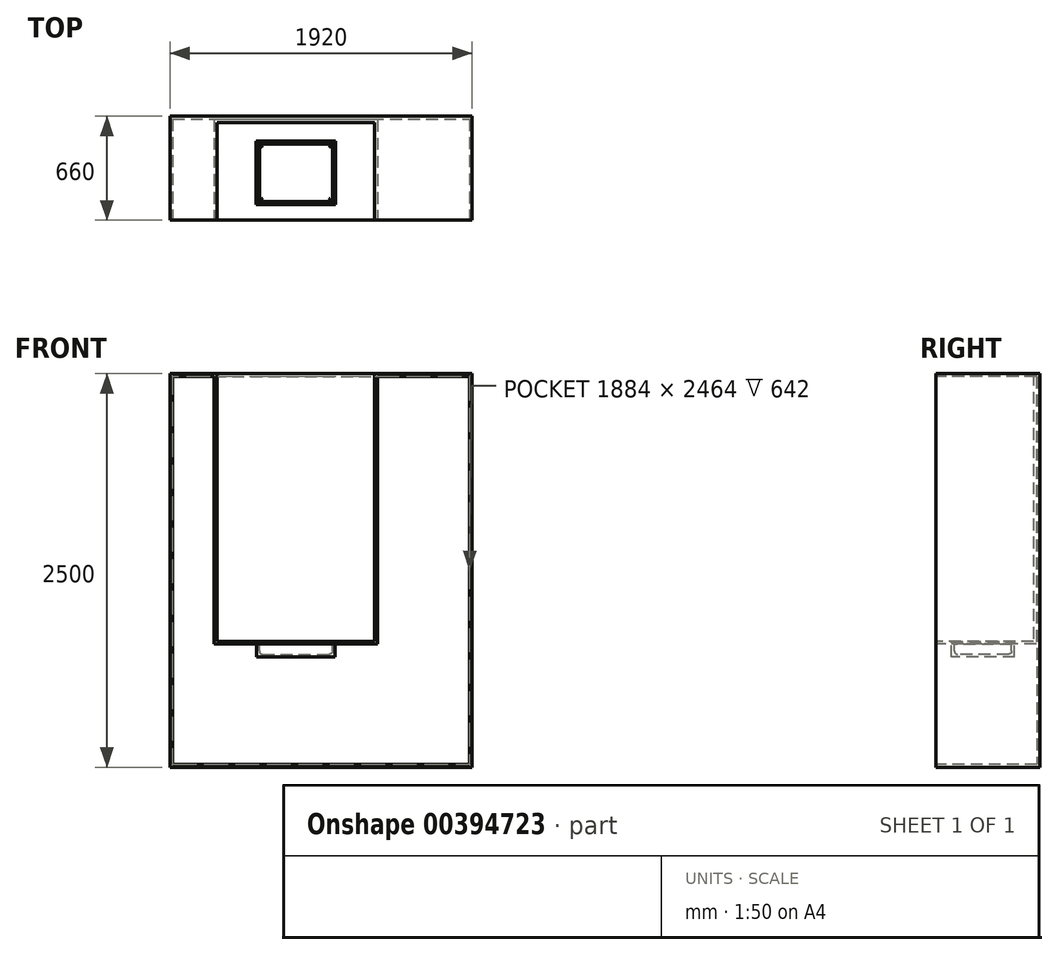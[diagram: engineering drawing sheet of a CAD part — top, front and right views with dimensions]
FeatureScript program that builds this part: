
annotation { "Feature Type Name" : "Feature", "Feature Type Description" : "" }
export const myFeature = defineFeature(function(context is Context, id is Id, definition is map)
    precondition{}
    {
        {
            var Q0;
            Q0=qCreatedBy(makeId("Top.planeOp"),FACE);
            var sketch = newSketch(context, id + "F0", { "sketchPlane" : qUnion([Q0])});
            skLineSegment(sketch, "E0.bottom", {"start": v(-310, 330) * mm, "end": v(310, 330) * mm});
            skLineSegment(sketch, "E0.top", {"start": v(-310, -330) * mm, "end": v(310, -330) * mm});
            skLineSegment(sketch, "E0.left", {"start": v(-310, 330) * mm, "end": v(-310, -330) * mm});
            skLineSegment(sketch, "E0.right", {"start": v(310, 330) * mm, "end": v(310, -330) * mm});
            skPoint(sketch, "E0.middle", {"position": v(0, 0) * mm});
            skLineSegment(sketch, "E1.bottom", {"start": v(-310, 330) * mm, "end": v(-1310, 330) * mm});
            skLineSegment(sketch, "E1.top", {"start": v(-310, -330) * mm, "end": v(-1310, -330) * mm});
            skLineSegment(sketch, "E1.right", {"start": v(-1310, 330) * mm, "end": v(-1310, -330) * mm});
            skLineSegment(sketch, "E2.bottom", {"start": v(-1310, 330) * mm, "end": v(-1610, 330) * mm});
            skLineSegment(sketch, "E2.top", {"start": v(-1310, -330) * mm, "end": v(-1610, -330) * mm});
            skLineSegment(sketch, "E2.right", {"start": v(-1610, 330) * mm, "end": v(-1610, -330) * mm});
            skSolve(sketch);
        }
        {
            var Q0;
            Q0=makeQuery(id+"F0.imprint","IMPRINT",FACE,{"disambiguationData":[TD([[makeQuery(id+"F0.imprint","IMPRINT",EDGE,{"derivedFrom":sQuery(id+"F0.wireOp",EDGE,"E0.bottom")}),-1.0]])]});
            extrude(context, id + "F1", {"entities" : qUnion([Q0]), "depth" : 2500 * mm});
        }
        {
            var Q0;
            Q0=makeQuery(id+"F0.imprint","IMPRINT",FACE,{"disambiguationData":[TD([[makeQuery(id+"F0.imprint","IMPRINT",EDGE,{"derivedFrom":sQuery(id+"F0.wireOp",EDGE,"E1.bottom")}),1.0]])]});
            extrude(context, id + "F2", {"entities" : qUnion([Q0]), "operationType" : NewBodyOperationType.ADD, "depth" : 800 * mm});
        }
        {
            var Q0;
            Q0=makeQuery(id+"F0.imprint","IMPRINT",FACE,{"disambiguationData":[TD([[makeQuery(id+"F0.imprint","IMPRINT",EDGE,{"derivedFrom":sQuery(id+"F0.wireOp",EDGE,"E2.bottom")}),1.0]])]});
            extrude(context, id + "F3", {"entities" : qUnion([Q0]), "operationType" : NewBodyOperationType.ADD, "depth" : 2500 * mm});
        }
        {
            var Q0;
            Q0=makeQuery(id+"F2.opExtrude","CAP_FACE",FACE,{"disambiguationData":[OSD([sQuery(id+"F0.wireOp",EDGE,"E1.bottom"),sQuery(id+"F0.wireOp",EDGE,"E1.top"),sQuery(id+"F0.wireOp",EDGE,"E0.left"),sQuery(id+"F0.wireOp",EDGE,"E1.right")])],"isStart":false});
            var sketch = newSketch(context, id + "F4", { "sketchPlane" : qUnion([Q0])});
            skLineSegment(sketch, "E3.bottom", {"start": v(-310, 330) * mm, "end": v(-1310, 330) * mm});
            skLineSegment(sketch, "E3.top", {"start": v(-310, 290) * mm, "end": v(-1310, 290) * mm});
            skLineSegment(sketch, "E3.left", {"start": v(-310, 330) * mm, "end": v(-310, 290) * mm});
            skLineSegment(sketch, "E3.right", {"start": v(-1310, 330) * mm, "end": v(-1310, 290) * mm});
            skSolve(sketch);
        }
        {
            var Q0;
            Q0=makeQuery(id+"F4.imprint","IMPRINT",FACE,{"disambiguationData":[TD([[makeQuery(id+"F4.imprint","IMPRINT",EDGE,{"derivedFrom":sQuery(id+"F4.wireOp",EDGE,"E3.bottom")}),1.0]])]});
            extrude(context, id + "F5", {"entities" : qUnion([Q0]), "operationType" : NewBodyOperationType.ADD, "depth" : 1700 * mm});
        }
        {
            var Q0;
            Q0=makeQuery(id+"F3.boolean.opBoolean","MERGE",FACE,{"derivedFrom":[makeQuery(id+"F2.boolean.opBoolean","MERGE",FACE,{"derivedFrom":[makeQuery(id+"F1.opExtrude","SWEPT_FACE",FACE,{"disambiguationData":[OSD([sQuery(id+"F0.wireOp",EDGE,"E0.top")])]}),makeQuery(id+"F2.opExtrude","SWEPT_FACE",FACE,{"disambiguationData":[OSD([sQuery(id+"F0.wireOp",EDGE,"E1.top")])]})]}),makeQuery(id+"F3.opExtrude","SWEPT_FACE",FACE,{"disambiguationData":[OSD([sQuery(id+"F0.wireOp",EDGE,"E2.top")])]})]});
            shell(context, id + "F6", {"entities" : qUnion([Q0]), "thickness" : 18 * mm});
        }
        {
            var Q0;
            Q0=makeQuery(id+"F2.opExtrude","CAP_FACE",FACE,{"disambiguationData":[OSD([sQuery(id+"F0.wireOp",EDGE,"E1.bottom"),sQuery(id+"F0.wireOp",EDGE,"E1.top"),sQuery(id+"F0.wireOp",EDGE,"E0.left"),sQuery(id+"F0.wireOp",EDGE,"E1.right")])],"isStart":false});
            var sketch = newSketch(context, id + "F7", { "sketchPlane" : qUnion([Q0])});
            skLineSegment(sketch, "E4.bottom", {"start": v(-1060, 170) * mm, "end": v(-560, 170) * mm});
            skLineSegment(sketch, "E4.top", {"start": v(-1060, -230) * mm, "end": v(-560, -230) * mm});
            skLineSegment(sketch, "E4.left", {"start": v(-1060, 170) * mm, "end": v(-1060, -230) * mm});
            skLineSegment(sketch, "E4.right", {"start": v(-560, 170) * mm, "end": v(-560, -230) * mm});
            skSolve(sketch);
        }
        {
            var Q0;
            Q0=makeQuery(id+"F7.imprint","IMPRINT",FACE,{"disambiguationData":[TD([[makeQuery(id+"F7.imprint","IMPRINT",EDGE,{"derivedFrom":sQuery(id+"F7.wireOp",EDGE,"E4.bottom")}),-1.0]])]});
            extrude(context, id + "F8", {"entities" : qUnion([Q0]), "operationType" : NewBodyOperationType.ADD, "oppositeDirection" : true, "depth" : 100 * mm});
        }
        {
            var Q0;
            Q0=makeQuery(id+"F2.opExtrude","CAP_FACE",FACE,{"disambiguationData":[OSD([sQuery(id+"F0.wireOp",EDGE,"E1.bottom"),sQuery(id+"F0.wireOp",EDGE,"E1.top"),sQuery(id+"F0.wireOp",EDGE,"E0.left"),sQuery(id+"F0.wireOp",EDGE,"E1.right")])],"isStart":false});
            shell(context, id + "F9", {"entities" : qUnion([Q0]), "thickness" : 18 * mm});
        }
        {
            var Q0;
            Q0=makeQuery(id+"F9.opShell","OFFSET_EDGE",EDGE,{"disambiguationData":[OSD([sQuery(id+"F0.wireOp",EDGE,"E1.bottom"),sQuery(id+"F0.wireOp",EDGE,"E1.top"),sQuery(id+"F0.wireOp",EDGE,"E0.left"),sQuery(id+"F0.wireOp",EDGE,"E1.right"),sQuery(id+"F7.wireOp",EDGE,"E4.bottom")])]});
            var Q1;
            Q1=makeQuery(id+"F9.opShell","OFFSET_EDGE",EDGE,{"disambiguationData":[OSD([sQuery(id+"F0.wireOp",EDGE,"E1.bottom"),sQuery(id+"F0.wireOp",EDGE,"E1.top"),sQuery(id+"F0.wireOp",EDGE,"E0.left"),sQuery(id+"F0.wireOp",EDGE,"E1.right"),sQuery(id+"F7.wireOp",EDGE,"E4.top")])]});
            var Q2;
            Q2=makeQuery(id+"F9.opShell","OFFSET_EDGE",EDGE,{"disambiguationData":[OSD([sQuery(id+"F0.wireOp",EDGE,"E1.bottom"),sQuery(id+"F0.wireOp",EDGE,"E1.top"),sQuery(id+"F0.wireOp",EDGE,"E0.left"),sQuery(id+"F0.wireOp",EDGE,"E1.right"),sQuery(id+"F7.wireOp",EDGE,"E4.right")])]});
            var Q3;
            Q3=makeQuery(id+"F9.opShell","OFFSET_EDGE",EDGE,{"disambiguationData":[OSD([sQuery(id+"F0.wireOp",EDGE,"E1.bottom"),sQuery(id+"F0.wireOp",EDGE,"E1.top"),sQuery(id+"F0.wireOp",EDGE,"E0.left"),sQuery(id+"F0.wireOp",EDGE,"E1.right"),sQuery(id+"F7.wireOp",EDGE,"E4.left")])]});
            chamfer(context, id + "F10", {"entities" : qUnion([Q0, Q1, Q2, Q3]), "width" : 20 * mm, "tangentPropagation" : true});
        }
        {
            var Q0;
            Q0=makeQuery(id+"F9.opShell","OFFSET_EDGE",EDGE,{"disambiguationData":[OSD([sQuery(id+"F7.wireOp",EDGE,"E4.bottom")])]});
            var Q1;
            Q1=makeQuery(id+"F9.opShell","OFFSET_FACE",FACE,{"disambiguationData":[OSD([sQuery(id+"F7.wireOp",EDGE,"E4.bottom"),sQuery(id+"F7.wireOp",EDGE,"E4.top"),sQuery(id+"F7.wireOp",EDGE,"E4.left"),sQuery(id+"F7.wireOp",EDGE,"E4.right")])]});
            fillet(context, id + "F11", {"entities" : qUnion([Q0, Q1]), "radius" : 20 * mm, "tangentPropagation" : true, "allowEdgeOverflow" : false});
        }
    });
